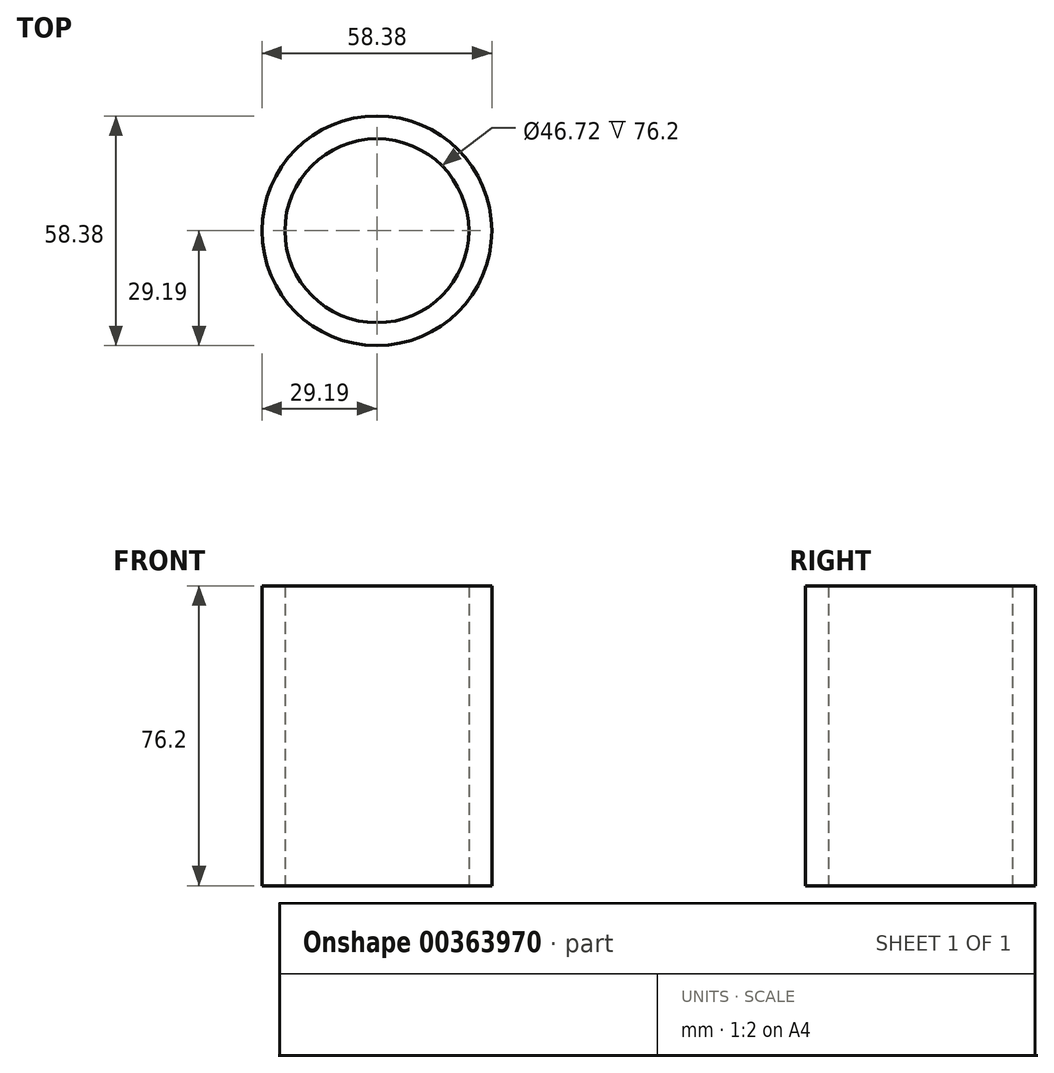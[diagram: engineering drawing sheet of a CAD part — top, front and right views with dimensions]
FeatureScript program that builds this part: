
annotation { "Feature Type Name" : "Feature", "Feature Type Description" : "" }
export const myFeature = defineFeature(function(context is Context, id is Id, definition is map)
    precondition{}
    {
        {
            var Q0;
            Q0=qCreatedBy(makeId("Top.planeOp"),FACE);
            var sketch = newSketch(context, id + "F0", { "sketchPlane" : qUnion([Q0])});
            skCircle(sketch, "E0", {"center": v(0, 0) * mm, "radius": 23.36 * mm});
            skCircle(sketch, "E1", {"center": v(0, 0) * mm, "radius": 29.19 * mm});
            skSolve(sketch);
        }
        {
            var Q0;
            Q0 = qSketchRegion(id + "F0", true);
            extrude(context, id + "F1", {"entities" : qUnion([Q0]), "depth" : 76.2 * mm});
        }
    });
